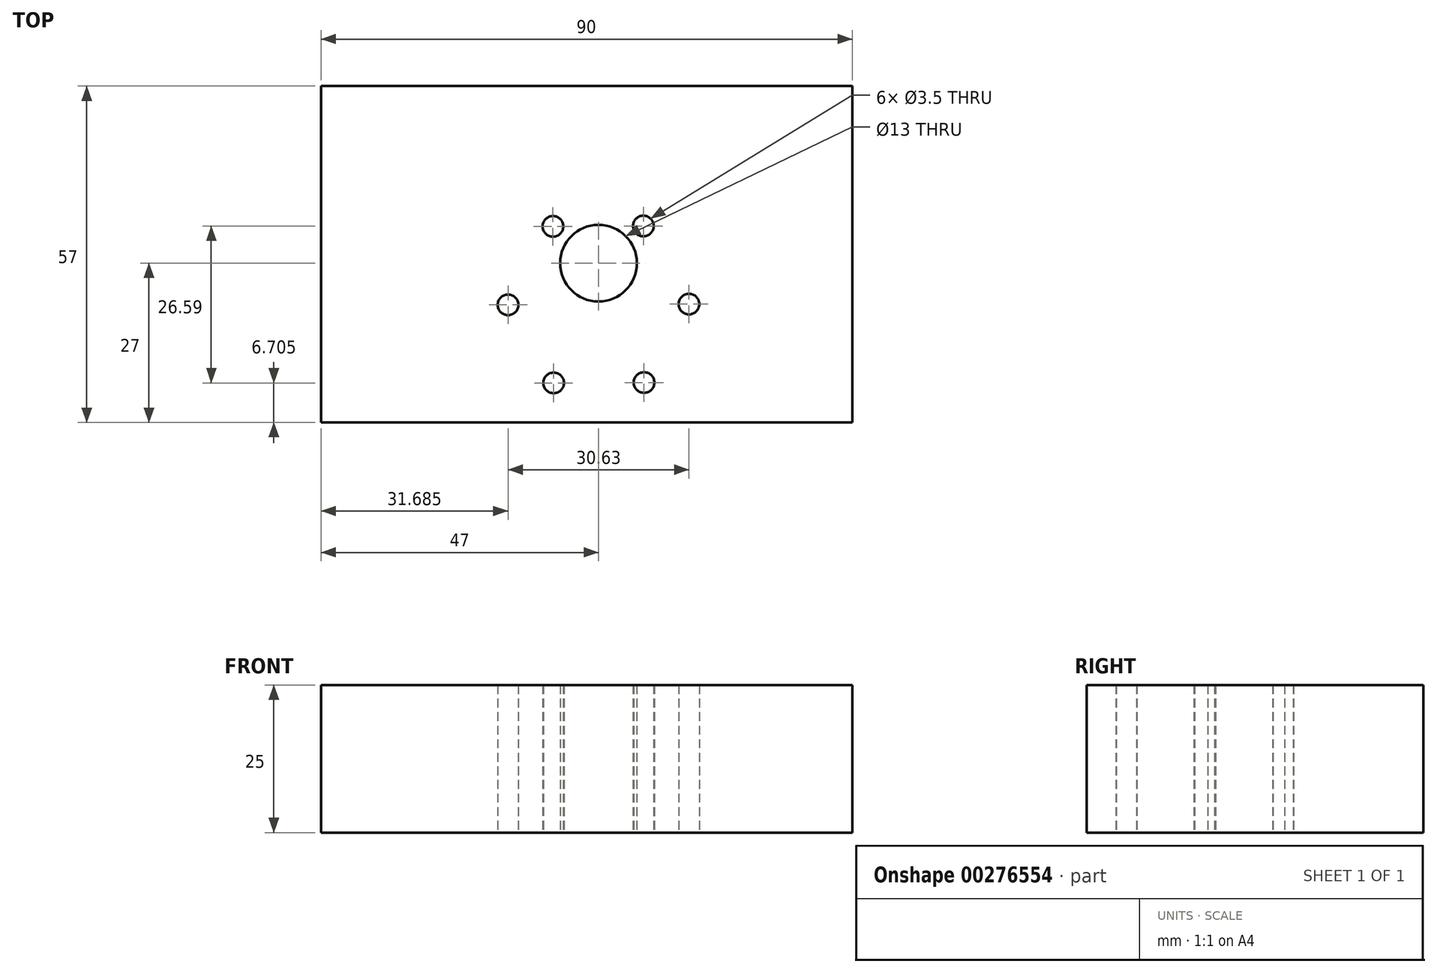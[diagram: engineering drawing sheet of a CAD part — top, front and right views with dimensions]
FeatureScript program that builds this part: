
annotation { "Feature Type Name" : "Feature", "Feature Type Description" : "" }
export const myFeature = defineFeature(function(context is Context, id is Id, definition is map)
    precondition{}
    {
        {
            var Q0;
            Q0=qCreatedBy(makeId("Top.planeOp"),FACE);
            var sketch = newSketch(context, id + "F0", { "sketchPlane" : qUnion([Q0])});
            skLineSegment(sketch, "E0.bottom", {"start": v(41, -29.1) * mm, "end": v(-49, -29.1) * mm});
            skLineSegment(sketch, "E0.top", {"start": v(41, 27.9) * mm, "end": v(-49, 27.9) * mm});
            skLineSegment(sketch, "E0.left", {"start": v(41, -29.1) * mm, "end": v(41, 27.9) * mm});
            skLineSegment(sketch, "E0.right", {"start": v(-49, -29.1) * mm, "end": v(-49, 27.9) * mm});
            skPoint(sketch, "E0.middle", {"position": v(-4, -0.6) * mm});
            skCircle(sketch, "E1", {"center": v(-9.71, 4.13) * mm, "radius": 1.75 * mm});
            skCircle(sketch, "E2.1.0", {"center": v(-17.31, -9.16) * mm, "radius": 1.75 * mm});
            skCircle(sketch, "E2.2.0", {"center": v(-9.6, -22.4) * mm, "radius": 1.75 * mm});
            skCircle(sketch, "E2.3.0", {"center": v(5.71, -22.33) * mm, "radius": 1.75 * mm});
            skCircle(sketch, "E2.4.0", {"center": v(13.31, -9.04) * mm, "radius": 1.75 * mm});
            skCircle(sketch, "E2.5.0", {"center": v(5.6, 4.2) * mm, "radius": 1.75 * mm});
            skPoint(sketch, "E2.center", {"position": v(-2, -9.1) * mm});
            skLineSegment(sketch, "E3", {"start": v(-2, -9.1) * mm, "end": v(-17.31, -9.16) * mm});
            skLineSegment(sketch, "E4", {"start": v(-2, -9.1) * mm, "end": v(-4, -0.6) * mm});
            skCircle(sketch, "E5", {"center": v(-2, -2.1) * mm, "radius": 6.5 * mm});
            skSolve(sketch);
        }
        {
            var Q0;
            Q0 = qSketchRegion(id + "F0", true);
            extrude(context, id + "F1", {"entities" : qUnion([Q0]), "depth" : 25 * mm, "offsetDistance" : 25 * mm});
        }
    });
